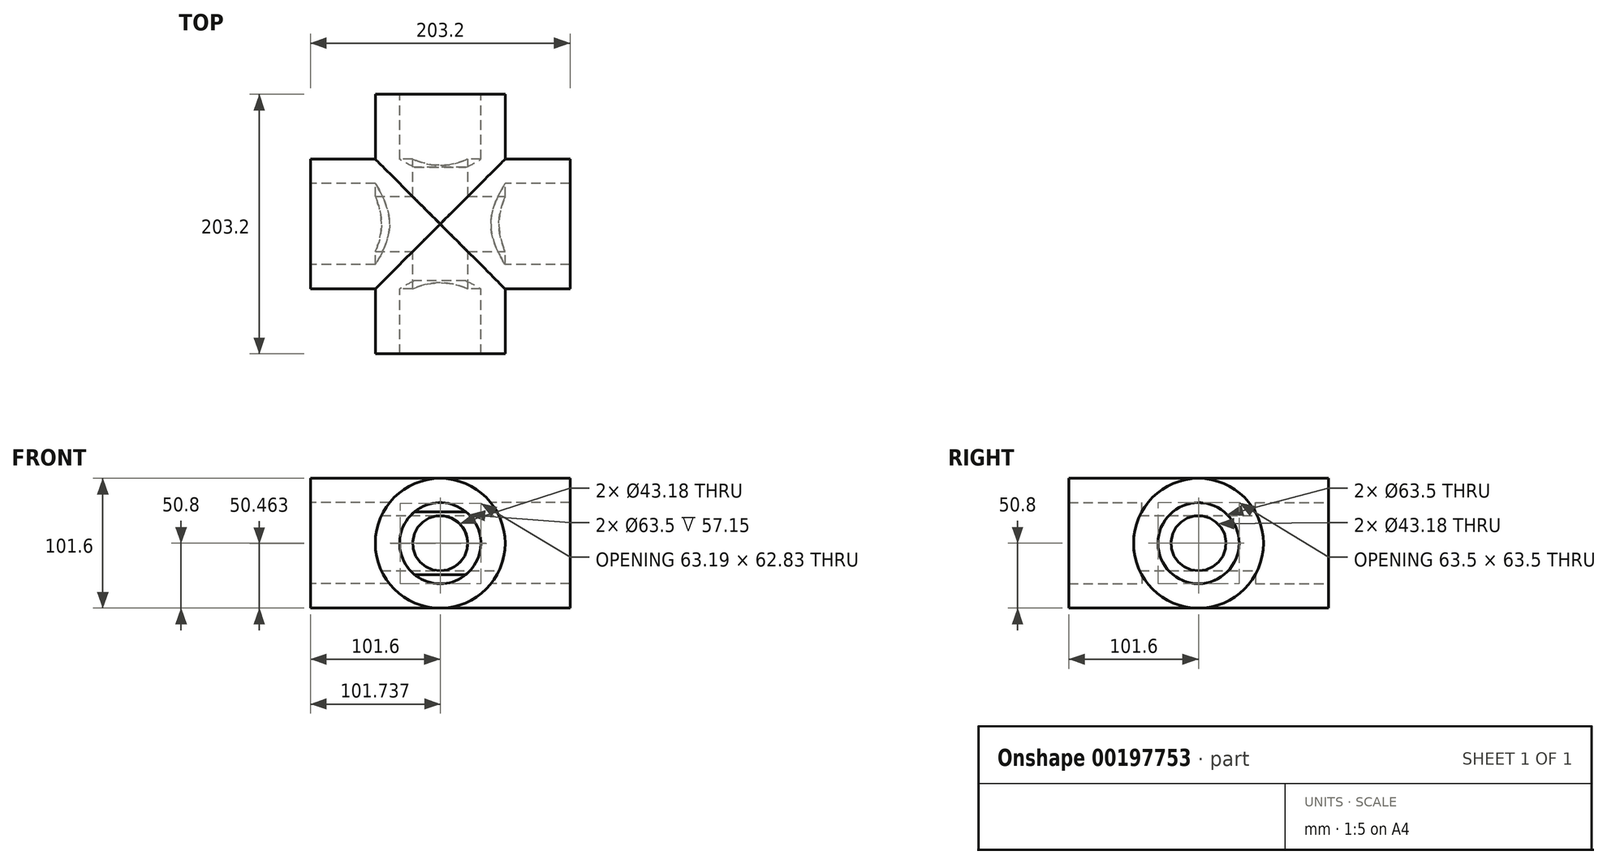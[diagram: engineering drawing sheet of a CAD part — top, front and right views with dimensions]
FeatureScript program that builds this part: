
annotation { "Feature Type Name" : "Feature", "Feature Type Description" : "" }
export const myFeature = defineFeature(function(context is Context, id is Id, definition is map)
    precondition{}
    {
        {
            var Q0;
            Q0=qCreatedBy(makeId("Front.planeOp"),FACE);
            var sketch = newSketch(context, id + "F0", { "sketchPlane" : qUnion([Q0])});
            skCircle(sketch, "E0", {"center": v(0, 0) * mm, "radius": 21.59 * mm});
            skCircle(sketch, "E1", {"center": v(0, 0) * mm, "radius": 31.75 * mm});
            skCircle(sketch, "E2", {"center": v(0, 0) * mm, "radius": 50.8 * mm});
            skSolve(sketch);
        }
        {
            var Q0;
            Q0=makeQuery(id+"F0.imprint","IMPRINT",FACE,{"disambiguationData":[TD([[makeQuery(id+"F0.imprint","IMPRINT",EDGE,{"derivedFrom":sQuery(id+"F0.wireOp",EDGE,"E0")}),-1.0]])]});
            extrude(context, id + "F1", {"entities" : qUnion([Q0]), "depth" : 88.9 * mm, "symmetric" : true});
        }
        {
            var Q0;
            Q0=qSketchRegion(id+"F0",true);
            var Q1;
            Q1=makeQuery(id+"F0.imprint","IMPRINT",FACE,{"disambiguationData":[TD([[makeQuery(id+"F0.imprint","IMPRINT",EDGE,{"derivedFrom":sQuery(id+"F0.wireOp",EDGE,"E1")}),-1.0]])]});
            extrude(context, id + "F2", {"entities" : qUnion([Q0, Q1]), "operationType" : NewBodyOperationType.ADD, "depth" : 203.2 * mm, "symmetric" : true});
        }
        {
            var Q0;
            Q0=qCreatedBy(makeId("Right.planeOp"),FACE);
            var sketch = newSketch(context, id + "F3", { "sketchPlane" : qUnion([Q0])});
            skCircle(sketch, "E3", {"center": v(0, 0) * mm, "radius": 21.59 * mm});
            skCircle(sketch, "E4", {"center": v(0, 0) * mm, "radius": 31.75 * mm});
            skCircle(sketch, "E5", {"center": v(0, 0) * mm, "radius": 50.8 * mm});
            skSolve(sketch);
        }
        {
            var Q0;
            Q0 = qSketchRegion(id + "F3", true);
            extrude(context, id + "F4", {"entities" : qUnion([Q0]), "depth" : 203.2 * mm, "symmetric" : true});
        }
        {
            var Q0;
            Q0=makeQuery(id+"F3.imprint","IMPRINT",FACE,{"disambiguationData":[TD([[makeQuery(id+"F3.imprint","IMPRINT",EDGE,{"derivedFrom":sQuery(id+"F3.wireOp",EDGE,"E3")}),-1.0]])]});
            extrude(context, id + "F5", {"entities" : qUnion([Q0]), "operationType" : NewBodyOperationType.ADD, "depth" : 76.2 * mm, "symmetric" : true});
        }
        {
            var Q0;
            Q0=makeQuery(id+"F0.imprint","IMPRINT",FACE,{"disambiguationData":[TD([[makeQuery(id+"F0.imprint","IMPRINT",EDGE,{"derivedFrom":sQuery(id+"F0.wireOp",EDGE,"E0")}),1.0]])]});
            extrude(context, id + "F6", {"entities" : qUnion([Q0]), "operationType" : NewBodyOperationType.REMOVE, "oppositeDirection" : true, "depth" : 254 * mm, "symmetric" : true});
        }
        {
            var Q0;
            Q0=makeQuery(id+"F3.imprint","IMPRINT",FACE,{"disambiguationData":[TD([[makeQuery(id+"F3.imprint","IMPRINT",EDGE,{"derivedFrom":sQuery(id+"F3.wireOp",EDGE,"E3")}),1.0]])]});
            extrude(context, id + "F7", {"entities" : qUnion([Q0]), "operationType" : NewBodyOperationType.REMOVE, "oppositeDirection" : true, "depth" : 254 * mm, "symmetric" : true});
        }
    });
